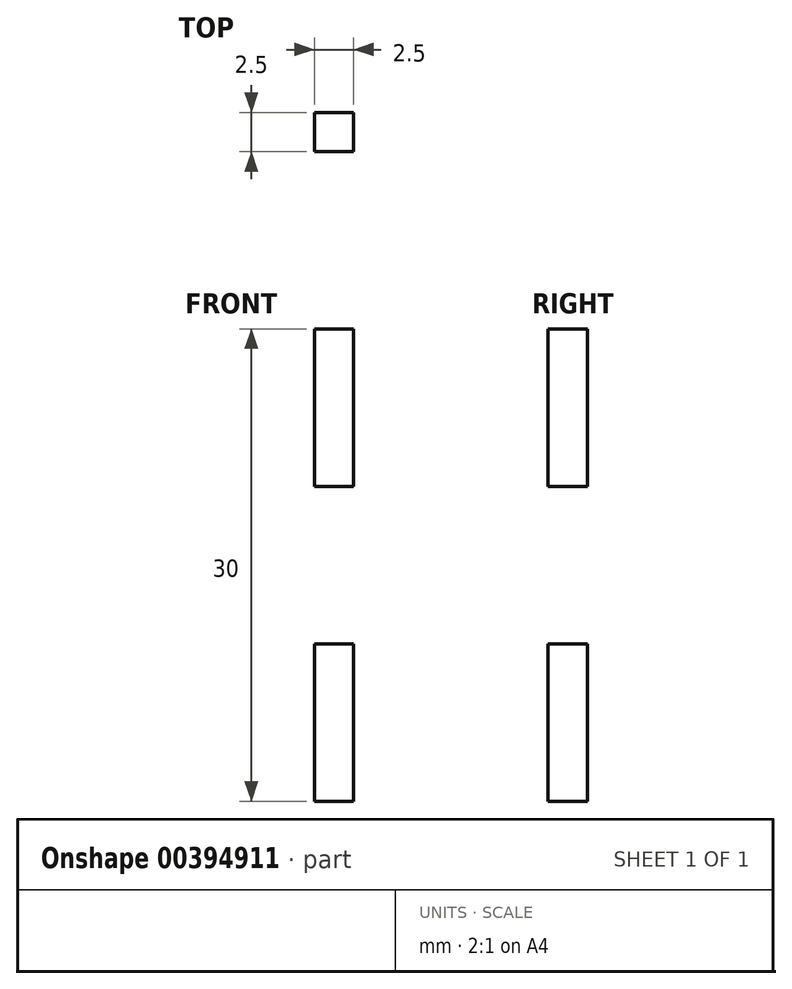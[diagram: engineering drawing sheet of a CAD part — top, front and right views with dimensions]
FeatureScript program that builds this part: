
annotation { "Feature Type Name" : "Feature", "Feature Type Description" : "" }
export const myFeature = defineFeature(function(context is Context, id is Id, definition is map)
    precondition{}
    {
        {
            var Q0;
            Q0=qCreatedBy(makeId("Front.planeOp"),FACE);
            var sketch = newSketch(context, id + "F0", { "sketchPlane" : qUnion([Q0])});
            skLineSegment(sketch, "E0.bottom", {"start": v(55, 15) * mm, "end": v(-55, 15) * mm});
            skLineSegment(sketch, "E0.top", {"start": v(55, -15) * mm, "end": v(-55, -15) * mm});
            skLineSegment(sketch, "E0.left", {"start": v(55, 15) * mm, "end": v(55, -15) * mm});
            skLineSegment(sketch, "E0.right", {"start": v(-55, 15) * mm, "end": v(-55, -15) * mm});
            skPoint(sketch, "E0.middle", {"position": v(0, 0) * mm});
            skLineSegment(sketch, "E1", {"start": v(-55, -15) * mm, "end": v(-55, -15) * mm});
            skLineSegment(sketch, "E2.bottom", {"start": v(-55, -15) * mm, "end": v(-45, -15) * mm});
            skLineSegment(sketch, "E2.top", {"start": v(-55, -12.5) * mm, "end": v(-45, -12.5) * mm});
            skLineSegment(sketch, "E2.left", {"start": v(-55, -15) * mm, "end": v(-55, -12.5) * mm});
            skLineSegment(sketch, "E2.right", {"start": v(-45, -15) * mm, "end": v(-45, -12.5) * mm});
            skLineSegment(sketch, "E3.0.1.0", {"start": v(-55, 15) * mm, "end": v(-45, 15) * mm});
            skLineSegment(sketch, "E3.0.1.1", {"start": v(-55, 12.5) * mm, "end": v(-45, 12.5) * mm});
            skLineSegment(sketch, "E3.0.1.2", {"start": v(-45, 12.5) * mm, "end": v(-45, 15) * mm});
            skLineSegment(sketch, "E3.0.1.3", {"start": v(-55, 12.5) * mm, "end": v(-55, 15) * mm});
            skLineSegment(sketch, "E3.1.0.0", {"start": v(-35, -12.5) * mm, "end": v(-25, -12.5) * mm});
            skLineSegment(sketch, "E3.1.0.1", {"start": v(-35, -15) * mm, "end": v(-25, -15) * mm});
            skLineSegment(sketch, "E3.1.0.2", {"start": v(-25, -15) * mm, "end": v(-25, -12.5) * mm});
            skLineSegment(sketch, "E3.1.0.3", {"start": v(-35, -15) * mm, "end": v(-35, -12.5) * mm});
            skLineSegment(sketch, "E3.1.1.0", {"start": v(-35, 15) * mm, "end": v(-25, 15) * mm});
            skLineSegment(sketch, "E3.1.1.1", {"start": v(-35, 12.5) * mm, "end": v(-25, 12.5) * mm});
            skLineSegment(sketch, "E3.1.1.2", {"start": v(-25, 12.5) * mm, "end": v(-25, 15) * mm});
            skLineSegment(sketch, "E3.1.1.3", {"start": v(-35, 12.5) * mm, "end": v(-35, 15) * mm});
            skLineSegment(sketch, "E3.2.0.0", {"start": v(-15, -12.5) * mm, "end": v(-5, -12.5) * mm});
            skLineSegment(sketch, "E3.2.0.1", {"start": v(-15, -15) * mm, "end": v(-5, -15) * mm});
            skLineSegment(sketch, "E3.2.0.2", {"start": v(-5, -15) * mm, "end": v(-5, -12.5) * mm});
            skLineSegment(sketch, "E3.2.0.3", {"start": v(-15, -15) * mm, "end": v(-15, -12.5) * mm});
            skLineSegment(sketch, "E3.2.1.0", {"start": v(-15, 15) * mm, "end": v(-5, 15) * mm});
            skLineSegment(sketch, "E3.2.1.1", {"start": v(-15, 12.5) * mm, "end": v(-5, 12.5) * mm});
            skLineSegment(sketch, "E3.2.1.2", {"start": v(-5, 12.5) * mm, "end": v(-5, 15) * mm});
            skLineSegment(sketch, "E3.2.1.3", {"start": v(-15, 12.5) * mm, "end": v(-15, 15) * mm});
            skLineSegment(sketch, "E3.3.0.0", {"start": v(5, -12.5) * mm, "end": v(15, -12.5) * mm});
            skLineSegment(sketch, "E3.3.0.1", {"start": v(5, -15) * mm, "end": v(15, -15) * mm});
            skLineSegment(sketch, "E3.3.0.2", {"start": v(15, -15) * mm, "end": v(15, -12.5) * mm});
            skLineSegment(sketch, "E3.3.0.3", {"start": v(5, -15) * mm, "end": v(5, -12.5) * mm});
            skLineSegment(sketch, "E3.3.1.0", {"start": v(5, 15) * mm, "end": v(15, 15) * mm});
            skLineSegment(sketch, "E3.3.1.1", {"start": v(5, 12.5) * mm, "end": v(15, 12.5) * mm});
            skLineSegment(sketch, "E3.3.1.2", {"start": v(15, 12.5) * mm, "end": v(15, 15) * mm});
            skLineSegment(sketch, "E3.3.1.3", {"start": v(5, 12.5) * mm, "end": v(5, 15) * mm});
            skLineSegment(sketch, "E3.4.0.0", {"start": v(25, -12.5) * mm, "end": v(35, -12.5) * mm});
            skLineSegment(sketch, "E3.4.0.1", {"start": v(25, -15) * mm, "end": v(35, -15) * mm});
            skLineSegment(sketch, "E3.4.0.2", {"start": v(35, -15) * mm, "end": v(35, -12.5) * mm});
            skLineSegment(sketch, "E3.4.0.3", {"start": v(25, -15) * mm, "end": v(25, -12.5) * mm});
            skLineSegment(sketch, "E3.4.1.0", {"start": v(25, 15) * mm, "end": v(35, 15) * mm});
            skLineSegment(sketch, "E3.4.1.1", {"start": v(25, 12.5) * mm, "end": v(35, 12.5) * mm});
            skLineSegment(sketch, "E3.4.1.2", {"start": v(35, 12.5) * mm, "end": v(35, 15) * mm});
            skLineSegment(sketch, "E3.4.1.3", {"start": v(25, 12.5) * mm, "end": v(25, 15) * mm});
            skLineSegment(sketch, "E3.direction1", {"start": v(-55, -12.5) * mm, "end": v(-35, -12.5) * mm, "construction": true});
            skLineSegment(sketch, "E3.direction2", {"start": v(-55, -12.5) * mm, "end": v(-55, 15) * mm, "construction": true});
            skLineSegment(sketch, "E4.0.5.0", {"start": v(45, -12.5) * mm, "end": v(55, -12.5) * mm});
            skLineSegment(sketch, "E4.3.5.0", {"start": v(45, -15) * mm, "end": v(55, -15) * mm});
            skLineSegment(sketch, "E4.6.5.0", {"start": v(55, -15) * mm, "end": v(55, -12.5) * mm});
            skLineSegment(sketch, "E4.9.5.0", {"start": v(45, -15) * mm, "end": v(45, -12.5) * mm});
            skLineSegment(sketch, "E4.0.5.1", {"start": v(45, 15) * mm, "end": v(55, 15) * mm});
            skLineSegment(sketch, "E4.3.5.1", {"start": v(45, 12.5) * mm, "end": v(55, 12.5) * mm});
            skLineSegment(sketch, "E4.6.5.1", {"start": v(55, 12.5) * mm, "end": v(55, 15) * mm});
            skLineSegment(sketch, "E4.9.5.1", {"start": v(45, 12.5) * mm, "end": v(45, 15) * mm});
            skLineSegment(sketch, "E5", {"start": v(55, 15) * mm, "end": v(55, 15) * mm});
            skLineSegment(sketch, "E6.bottom", {"start": v(55, 15) * mm, "end": v(52.5, 15) * mm});
            skLineSegment(sketch, "E6.top", {"start": v(55, 5) * mm, "end": v(52.5, 5) * mm});
            skLineSegment(sketch, "E6.left", {"start": v(55, 15) * mm, "end": v(55, 5) * mm});
            skLineSegment(sketch, "E6.right", {"start": v(52.5, 15) * mm, "end": v(52.5, 5) * mm});
            skLineSegment(sketch, "E7.0.1.0", {"start": v(52.5, -5) * mm, "end": v(52.5, -15) * mm});
            skLineSegment(sketch, "E7.0.1.1", {"start": v(55, -5) * mm, "end": v(52.5, -5) * mm});
            skLineSegment(sketch, "E7.0.1.2", {"start": v(55, -5) * mm, "end": v(55, -15) * mm});
            skLineSegment(sketch, "E7.0.1.3", {"start": v(55, -15) * mm, "end": v(52.5, -15) * mm});
            skLineSegment(sketch, "E7.1.0.0", {"start": v(-55, 15) * mm, "end": v(-55, 5) * mm});
            skLineSegment(sketch, "E7.1.0.1", {"start": v(-52.5, 15) * mm, "end": v(-55, 15) * mm});
            skLineSegment(sketch, "E7.1.0.2", {"start": v(-52.5, 15) * mm, "end": v(-52.5, 5) * mm});
            skLineSegment(sketch, "E7.1.0.3", {"start": v(-52.5, 5) * mm, "end": v(-55, 5) * mm});
            skLineSegment(sketch, "E7.1.1.0", {"start": v(-55, -5) * mm, "end": v(-55, -15) * mm});
            skLineSegment(sketch, "E7.1.1.1", {"start": v(-52.5, -5) * mm, "end": v(-55, -5) * mm});
            skLineSegment(sketch, "E7.1.1.2", {"start": v(-52.5, -5) * mm, "end": v(-52.5, -15) * mm});
            skLineSegment(sketch, "E7.1.1.3", {"start": v(-52.5, -15) * mm, "end": v(-55, -15) * mm});
            skLineSegment(sketch, "E7.direction1", {"start": v(52.5, 5) * mm, "end": v(-55, 5) * mm, "construction": true});
            skLineSegment(sketch, "E7.direction2", {"start": v(52.5, 5) * mm, "end": v(52.5, -15) * mm, "construction": true});
            skSolve(sketch);
        }
        {
            var Q0;
            {var subQ5=sQuery(id+"F0.wireOp",EDGE,"E0.left");Q0=makeQuery(id+"F0.imprint","IMPRINT",FACE,{"disambiguationData":[TD([[makeQuery(id+"F0.imprint","IMPRINT",EDGE,{"derivedFrom":subQ5}),-1.0]])]});}
            extrude(context, id + "F1", {"entities" : qUnion([Q0]), "depth" : 2.5 * mm});
        }
    });
